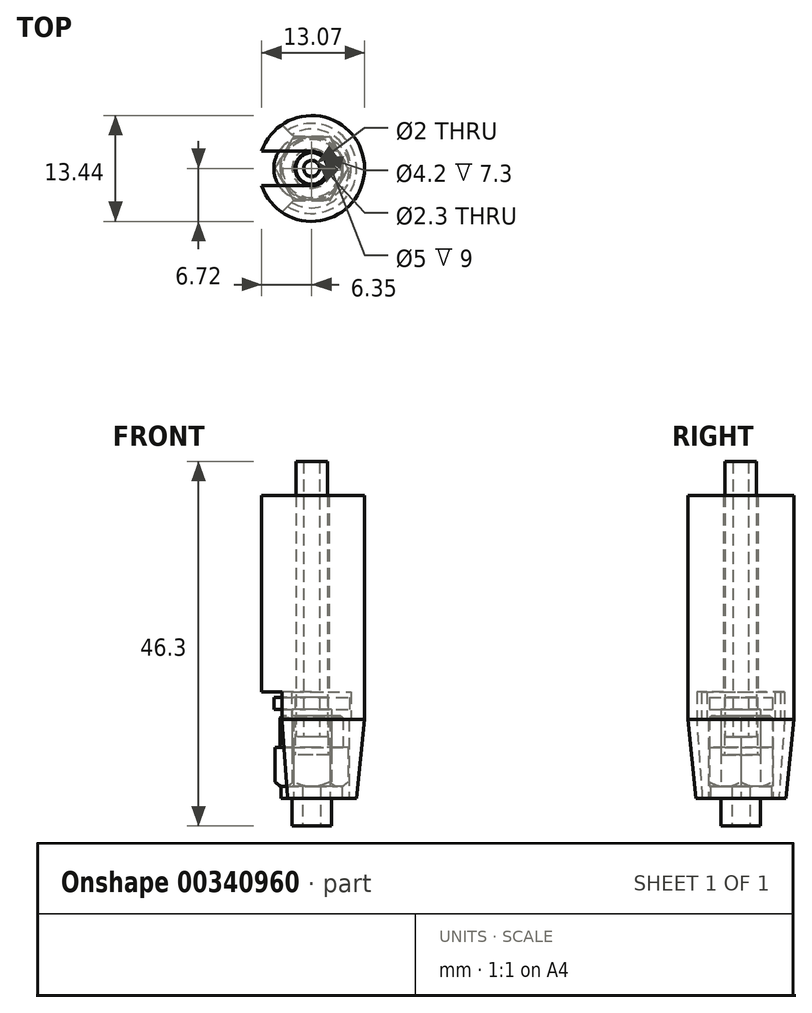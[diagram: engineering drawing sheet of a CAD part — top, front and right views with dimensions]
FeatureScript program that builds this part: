
annotation { "Feature Type Name" : "Feature", "Feature Type Description" : "" }
export const myFeature = defineFeature(function(context is Context, id is Id, definition is map)
    precondition{}
    {
        {
            var Q0;
            Q0=qCreatedBy(makeId("Top.planeOp"),FACE);
            var sketch = newSketch(context, id + "F0", { "sketchPlane" : qUnion([Q0])});
            skCircle(sketch, "E0", {"center": v(0, 0) * mm, "radius": 2.5 * mm});
            skCircle(sketch, "E1", {"center": v(0, 0) * mm, "radius": 1.15 * mm});
            skSolve(sketch);
        }
        {
            var Q0;
            Q0 = qSketchRegion(id + "F0", true);
            extrude(context, id + "F1", {"entities" : qUnion([Q0]), "depth" : 3.5 * mm});
        }
        {
            var Q0;
            Q0=makeQuery(id+"F1.opExtrude","CAP_FACE",FACE,{"disambiguationData":[OSD([sQuery(id+"F0.wireOp",EDGE,"E0"),sQuery(id+"F0.wireOp",EDGE,"E1")])],"isStart":false});
            var sketch = newSketch(context, id + "F2", { "sketchPlane" : qUnion([Q0])});
            skCircle(sketch, "E2", {"center": v(0, 0) * mm, "radius": 3.88 * mm});
            skCircle(sketch, "E3.0", {"center": v(0, 0) * mm, "radius": 1.15 * mm});
            skSolve(sketch);
        }
        {
            var Q0;
            Q0 = qSketchRegion(id + "F2", true);
            extrude(context, id + "F3", {"entities" : qUnion([Q0]), "operationType" : NewBodyOperationType.ADD, "depth" : 1.5 * mm});
        }
        {
            var Q0;
            Q0=makeQuery(id+"F3.opExtrude","CAP_FACE",FACE,{"disambiguationData":[OSD([sQuery(id+"F2.wireOp",EDGE,"E2"),sQuery(id+"F2.wireOp",EDGE,"E3.0")])],"isStart":false});
            var sketch = newSketch(context, id + "F4", { "sketchPlane" : qUnion([Q0])});
            skCircle(sketch, "E4.cCircle", {"center": v(0, 0) * mm, "radius": 4 * mm, "construction": true});
            skLineSegment(sketch, "E4.0", {"start": v(4.62, 0) * mm, "end": v(2.3, -4) * mm});
            skLineSegment(sketch, "E4.1", {"start": v(2.3, -4) * mm, "end": v(-2.3, -4) * mm});
            skLineSegment(sketch, "E4.2", {"start": v(-2.3, -4) * mm, "end": v(-4.62, 0) * mm});
            skLineSegment(sketch, "E4.3", {"start": v(-4.62, 0) * mm, "end": v(-2.3, 4) * mm});
            skLineSegment(sketch, "E4.4", {"start": v(-2.3, 4) * mm, "end": v(2.3, 4) * mm});
            skLineSegment(sketch, "E4.5", {"start": v(2.3, 4) * mm, "end": v(4.62, 0) * mm});
            skPoint(sketch, "E4.0.midPoint", {"position": v(3.46, -2) * mm});
            skCircle(sketch, "E5", {"center": v(0, 0) * mm, "radius": 2.5 * mm});
            skSolve(sketch);
        }
        {
            var Q0;
            Q0 = qSketchRegion(id + "F4", true);
            extrude(context, id + "F5", {"entities" : qUnion([Q0]), "depth" : 5 * mm});
        }
        {
            var Q0;
            Q0=makeQuery(id+"F3.opExtrude","CAP_FACE",FACE,{"disambiguationData":[OSD([sQuery(id+"F2.wireOp",EDGE,"E2"),sQuery(id+"F2.wireOp",EDGE,"E3.0")])],"isStart":false});
            var sketch = newSketch(context, id + "F6", { "sketchPlane" : qUnion([Q0])});
            skCircle(sketch, "E6", {"center": v(0, 0) * mm, "radius": 4.62 * mm});
            skSolve(sketch);
        }
        {
            var Q0;
            Q0 = qSketchRegion(id + "F6", true);
            var Q1;
            Q1=makeQuery(id+"F5.opExtrude","CAP_FACE",FACE,{"disambiguationData":[OSD([sQuery(id+"F4.wireOp",EDGE,"E4.0"),sQuery(id+"F4.wireOp",EDGE,"E4.1"),sQuery(id+"F4.wireOp",EDGE,"E4.2"),sQuery(id+"F4.wireOp",EDGE,"E4.3"),sQuery(id+"F4.wireOp",EDGE,"E4.4"),sQuery(id+"F4.wireOp",EDGE,"E4.5"),sQuery(id+"F4.wireOp",EDGE,"E5")])],"isStart":false});
            extrude(context, id + "F7", {"entities" : qUnion([Q0]), "endBound" : BoundingType.UP_TO_SURFACE, "endBoundEntityFace" : qUnion([Q1]), "depth" : 25 * mm});
        }
        {
            var Q0;
            Q0=makeQuery(id+"F7.opExtrude","TWEAK_EDGE",EDGE,{"derivedFrom":[makeQuery(id+"F5.opExtrude","CAP_FACE",FACE,{"disambiguationData":[OSD([sQuery(id+"F4.wireOp",EDGE,"E4.0"),sQuery(id+"F4.wireOp",EDGE,"E4.1"),sQuery(id+"F4.wireOp",EDGE,"E4.2"),sQuery(id+"F4.wireOp",EDGE,"E4.3"),sQuery(id+"F4.wireOp",EDGE,"E4.4"),sQuery(id+"F4.wireOp",EDGE,"E4.5"),sQuery(id+"F4.wireOp",EDGE,"E5")])],"isStart":false}),makeQuery(id+"F6.imprint","IMPRINT",EDGE,{"derivedFrom":sQuery(id+"F6.wireOp",EDGE,"E6")})]});
            var Q1;
            Q1=makeQuery(id+"F7.opExtrude","CAP_EDGE",EDGE,{"disambiguationData":[OSD([sQuery(id+"F6.wireOp",EDGE,"E6")])],"isStart":true});
            chamfer(context, id + "F8", {"entities" : qUnion([Q0, Q1]), "width" : 0.6 * mm, "tangentPropagation" : true});
        }
        {
            var Q0;
            Q0=makeQuery(id+"F5.opExtrude","SWEPT_BODY",BODY,{"disambiguationData":[OSD([sQuery(id+"F4.wireOp",EDGE,"E4.0"),sQuery(id+"F4.wireOp",EDGE,"E4.1"),sQuery(id+"F4.wireOp",EDGE,"E4.2"),sQuery(id+"F4.wireOp",EDGE,"E4.3"),sQuery(id+"F4.wireOp",EDGE,"E4.4"),sQuery(id+"F4.wireOp",EDGE,"E4.5"),sQuery(id+"F4.wireOp",EDGE,"E5")])]});
            var Q1;
            Q1=makeQuery(id+"F7.opExtrude","SWEPT_BODY",BODY,{"disambiguationData":[OSD([sQuery(id+"F6.wireOp",EDGE,"E6")])]});
            booleanBodies(context, id + "F9", {"operationType" : BooleanOperationType.INTERSECTION, "tools" : qUnion([Q0, Q1])});
        }
        {
            var Q0;
            Q0=makeQuery(id+"F5.opExtrude","CAP_FACE",FACE,{"disambiguationData":[OSD([sQuery(id+"F4.wireOp",EDGE,"E4.0"),sQuery(id+"F4.wireOp",EDGE,"E4.1"),sQuery(id+"F4.wireOp",EDGE,"E4.2"),sQuery(id+"F4.wireOp",EDGE,"E4.3"),sQuery(id+"F4.wireOp",EDGE,"E4.4"),sQuery(id+"F4.wireOp",EDGE,"E4.5"),sQuery(id+"F4.wireOp",EDGE,"E5")])],"isStart":false});
            var sketch = newSketch(context, id + "F10", { "sketchPlane" : qUnion([Q0])});
            skCircle(sketch, "E7", {"center": v(0, 0) * mm, "radius": 4 * mm});
            skCircle(sketch, "E8.0", {"center": v(0, 0) * mm, "radius": 2.5 * mm});
            skSolve(sketch);
        }
        {
            var Q0;
            Q0 = qSketchRegion(id + "F10", true);
            extrude(context, id + "F11", {"entities" : qUnion([Q0]), "operationType" : NewBodyOperationType.ADD, "depth" : 4 * mm});
        }
        {
            var Q0;
            Q0=makeQuery(id+"F11.opExtrude","CAP_EDGE",EDGE,{"disambiguationData":[OSD([sQuery(id+"F10.wireOp",EDGE,"E7")])],"isStart":false});
            chamfer(context, id + "F12", {"entities" : qUnion([Q0]), "width" : 0.3 * mm, "tangentPropagation" : true});
        }
        {
            var Q0;
            Q0=makeQuery(id+"F1.opExtrude","SWEPT_BODY",BODY,{"disambiguationData":[OSD([sQuery(id+"F0.wireOp",EDGE,"E0"),sQuery(id+"F0.wireOp",EDGE,"E1")])]});
            var Q1;
            Q1=makeQuery(id+"F9.opBoolean","INTERSECT",BODY,{"derivedFrom":[makeQuery(id+"F5.opExtrude","SWEPT_BODY",BODY,{"disambiguationData":[OSD([sQuery(id+"F4.wireOp",EDGE,"E4.0"),sQuery(id+"F4.wireOp",EDGE,"E4.1"),sQuery(id+"F4.wireOp",EDGE,"E4.2"),sQuery(id+"F4.wireOp",EDGE,"E4.3"),sQuery(id+"F4.wireOp",EDGE,"E4.4"),sQuery(id+"F4.wireOp",EDGE,"E4.5"),sQuery(id+"F4.wireOp",EDGE,"E5")])]}),makeQuery(id+"F7.opExtrude","SWEPT_BODY",BODY,{"disambiguationData":[OSD([sQuery(id+"F6.wireOp",EDGE,"E6")])]})]});
            var Q2;
            Q2=makeQuery(id+"F11.opExtrude","SWEPT_BODY",BODY,{"disambiguationData":[OSD([sQuery(id+"F10.wireOp",EDGE,"E7"),sQuery(id+"F10.wireOp",EDGE,"E8.0")])]});
            booleanBodies(context, id + "F13", {"operationType" : BooleanOperationType.UNION, "tools" : qUnion([Q0, Q1, Q2])});
        }
        {
            var Q0;
            Q0=makeQuery(id+"F11.opExtrude","CAP_FACE",FACE,{"disambiguationData":[OSD([sQuery(id+"F10.wireOp",EDGE,"E7"),sQuery(id+"F10.wireOp",EDGE,"E8.0")])],"isStart":false});
            var sketch = newSketch(context, id + "F14", { "sketchPlane" : qUnion([Q0])});
            skCircle(sketch, "E9.0", {"center": v(0, 0) * mm, "radius": 2.5 * mm});
            skCircle(sketch, "E10", {"center": v(0, 0) * mm, "radius": 2.1 * mm});
            skSolve(sketch);
        }
        {
            var Q0;
            Q0 = qSketchRegion(id + "F14", true);
            extrude(context, id + "F15", {"entities" : qUnion([Q0]), "depth" : 0.8 * mm, "hasSecondDirection" : true, "secondDirectionOppositeDirection" : true, "secondDirectionDepth" : 5 * mm});
        }
        {
            var Q0;
            Q0=makeQuery(id+"F15.opExtrude","CAP_FACE",FACE,{"disambiguationData":[OSD([sQuery(id+"F14.wireOp",EDGE,"E9.0"),sQuery(id+"F14.wireOp",EDGE,"E10")])],"isStart":false});
            var sketch = newSketch(context, id + "F16", { "sketchPlane" : qUnion([Q0])});
            skLineSegment(sketch, "E11", {"start": v(0.8, 0) * mm, "end": v(-0.8, 0) * mm});
            skArc(sketch, "E12.0.startCap", {"start": v(0.8, 4) * mm, "mid": v(4.8, 0) * mm, "end": v(0.8, -4) * mm});
            skArc(sketch, "E12.0.endCap", {"start": v(-0.8, -4) * mm, "mid": v(-4.8, 0) * mm, "end": v(-0.8, 4) * mm});
            skLineSegment(sketch, "E12.0.left", {"start": v(0.8, -4) * mm, "end": v(-0.8, -4) * mm});
            skLineSegment(sketch, "E12.0.right", {"start": v(0.8, 4) * mm, "end": v(-0.8, 4) * mm});
            skPoint(sketch, "E13", {"position": v(4.8, 0) * mm});
            skPoint(sketch, "E14", {"position": v(-4.8, 0) * mm});
            skPoint(sketch, "E15", {"position": v(0, 0) * mm});
            skCircle(sketch, "E16.0", {"center": v(0, 0) * mm, "radius": 2.1 * mm});
            skSolve(sketch);
        }
        {
            var Q0;
            Q0 = qSketchRegion(id + "F16", true);
            extrude(context, id + "F17", {"entities" : qUnion([Q0]), "operationType" : NewBodyOperationType.ADD, "depth" : 1.5 * mm});
        }
        {
            var Q0;
            Q0=makeQuery(id+"F3.opExtrude","CAP_FACE",FACE,{"disambiguationData":[OSD([sQuery(id+"F2.wireOp",EDGE,"E2"),sQuery(id+"F2.wireOp",EDGE,"E3.0")])],"isStart":true});
            var sketch = newSketch(context, id + "F18", { "sketchPlane" : qUnion([Q0])});
            skLineSegment(sketch, "E17", {"start": v(-2.3, -4.1) * mm, "end": v(2.35, -4.1) * mm});
            skLineSegment(sketch, "E18", {"start": v(2.35, -4.1) * mm, "end": v(4.72, 0) * mm});
            skLineSegment(sketch, "E19.MirrorCS", {"start": v(-2.3, 4.1) * mm, "end": v(2.35, 4.1) * mm});
            skLineSegment(sketch, "E20.MirrorCS", {"start": v(2.35, 4.1) * mm, "end": v(4.72, 0) * mm});
            skArc(sketch, "E21", {"start": v(-3.77, -5.56) * mm, "mid": v(6.72, 0) * mm, "end": v(-3.77, 5.56) * mm});
            skLineSegment(sketch, "E22", {"start": v(-2.3, -4.1) * mm, "end": v(-3.77, -5.56) * mm});
            skLineSegment(sketch, "E23.MirrorCS", {"start": v(-2.3, 4.1) * mm, "end": v(-3.77, 5.56) * mm});
            skSolve(sketch);
        }
        {
            var Q0;
            Q0 = qSketchRegion(id + "F18", true);
            extrude(context, id + "F19", {"entities" : qUnion([Q0]), "oppositeDirection" : true, "depth" : 10 * mm});
        }
        {
            var Q0;
            Q0=makeQuery(id+"F19.opExtrude","CAP_EDGE",EDGE,{"disambiguationData":[OSD([sQuery(id+"F18.wireOp",EDGE,"E21")])],"isStart":true});
            chamfer(context, id + "F20", {"entities" : qUnion([Q0]), "chamferType" : ChamferType.TWO_OFFSETS, "width1" : 1 * mm, "oppositeDirection" : false, "width2" : 10 * mm, "tangentPropagation" : true});
        }
        {
            var Q0;
            Q0=makeQuery(id+"F19.opExtrude","CAP_FACE",FACE,{"disambiguationData":[OSD([sQuery(id+"F18.wireOp",EDGE,"E17"),sQuery(id+"F18.wireOp",EDGE,"E18"),sQuery(id+"F18.wireOp",EDGE,"E19.MirrorCS"),sQuery(id+"F18.wireOp",EDGE,"E20.MirrorCS"),sQuery(id+"F18.wireOp",EDGE,"E21"),sQuery(id+"F18.wireOp",EDGE,"E22"),sQuery(id+"F18.wireOp",EDGE,"E23.MirrorCS")])],"isStart":false});
            var sketch = newSketch(context, id + "F21", { "sketchPlane" : qUnion([Q0])});
            skArc(sketch, "E24.0", {"start": v(-3.77, 5.56) * mm, "mid": v(6.72, 0) * mm, "end": v(-3.77, -5.56) * mm});
            skLineSegment(sketch, "E25.0", {"start": v(-2.52, 4.32) * mm, "end": v(-3.77, 5.56) * mm});
            skLineSegment(sketch, "E26.0", {"start": v(-2.52, -4.32) * mm, "end": v(-3.77, -5.56) * mm});
            skArc(sketch, "E27", {"start": v(-2.52, 4.32) * mm, "mid": v(5, 0) * mm, "end": v(-2.52, -4.32) * mm});
            skPoint(sketch, "E28.orphan", {"position": v(-2.3, -4.1) * mm});
            skPoint(sketch, "E29.orphan", {"position": v(-2.3, 4.1) * mm});
            skSolve(sketch);
        }
        {
            var Q0;
            Q0 = qSketchRegion(id + "F21", true);
            extrude(context, id + "F22", {"entities" : qUnion([Q0]), "operationType" : NewBodyOperationType.ADD, "depth" : 3.5 * mm});
        }
        {
            var Q0;
            Q0=makeQuery(id+"F22.opExtrude","CAP_FACE",FACE,{"disambiguationData":[OSD([sQuery(id+"F21.wireOp",EDGE,"E24.0"),sQuery(id+"F21.wireOp",EDGE,"E25.0"),sQuery(id+"F21.wireOp",EDGE,"E26.0"),sQuery(id+"F21.wireOp",EDGE,"E27")])],"isStart":false});
            var sketch = newSketch(context, id + "F23", { "sketchPlane" : qUnion([Q0])});
            skArc(sketch, "E30", {"start": v(-6.35, 2.2) * mm, "mid": v(6.72, 0) * mm, "end": v(-6.35, -2.2) * mm});
            skArc(sketch, "E31", {"start": v(0, 2.2) * mm, "mid": v(2.2, 0) * mm, "end": v(0, -2.2) * mm});
            skLineSegment(sketch, "E32", {"start": v(0, 2.2) * mm, "end": v(-6.35, 2.2) * mm});
            skLineSegment(sketch, "E33.MirrorCS", {"start": v(0, -2.2) * mm, "end": v(-6.35, -2.2) * mm});
            skSolve(sketch);
        }
        {
            var Q0;
            Q0 = qSketchRegion(id + "F23", true);
            extrude(context, id + "F24", {"entities" : qUnion([Q0]), "operationType" : NewBodyOperationType.ADD, "depth" : 25 * mm});
        }
        {
            var Q0;
            Q0=makeQuery(id+"F17.opExtrude","CAP_FACE",FACE,{"disambiguationData":[OSD([sQuery(id+"F16.wireOp",EDGE,"E12.0.startCap"),sQuery(id+"F16.wireOp",EDGE,"E12.0.endCap"),sQuery(id+"F16.wireOp",EDGE,"E12.0.left"),sQuery(id+"F16.wireOp",EDGE,"E12.0.right"),sQuery(id+"F16.wireOp",EDGE,"E16.0")])],"isStart":false});
            var sketch = newSketch(context, id + "F25", { "sketchPlane" : qUnion([Q0])});
            skCircle(sketch, "E34", {"center": v(0, 0) * mm, "radius": 2 * mm});
            skCircle(sketch, "E35", {"center": v(0, 0) * mm, "radius": 1 * mm});
            skSolve(sketch);
        }
        {
            var Q0;
            Q0 = qSketchRegion(id + "F25", true);
            extrude(context, id + "F26", {"entities" : qUnion([Q0]), "depth" : 30 * mm, "hasSecondDirection" : true, "secondDirectionOppositeDirection" : true, "secondDirectionDepth" : 5 * mm});
        }
    });
